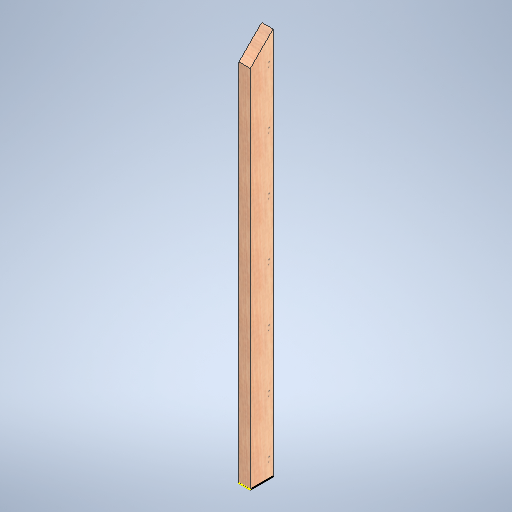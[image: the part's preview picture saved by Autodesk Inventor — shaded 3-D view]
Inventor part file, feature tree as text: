
AUTODESK INVENTOR PART (.ipt)
format: ipt  version: 2025 (Build 290162000, 162)  size: 309,760 bytes
history: native  units: in
note: dims shown in document units (in); Inventor stores cm internally (conversion verified against a paired STEP export)
features: sketch x3, extrude x2
ambient origin geometry x8: Origin, YZ Plane, XZ Plane, XY Plane, X Axis, Y Axis, Z Axis, Center Point
bodies: Solid1 (feature_tree)
feature tree (5):
  extrude  "Extrusion1"  Depth=4.0in
  extrude  "Extrusion2"  TaperAngle=45.0deg  [1 undecoded]
  sketch  "Sketch3"  dims[d5=2.0in d6=0.0in d7=0.5in d8=0.0344in]
  sketch  "Sketch1"  dims[d0=2.0in d1=4.0in]
  sketch  "Sketch2"  dims[d2=68.0in d3=0.0in d4=45.0deg]
note: 1 required parameter value undecoded (feature->parameter linkage not recoverable at this tier; creation-order binding heuristic only, values carry confidence <= 0.55)
